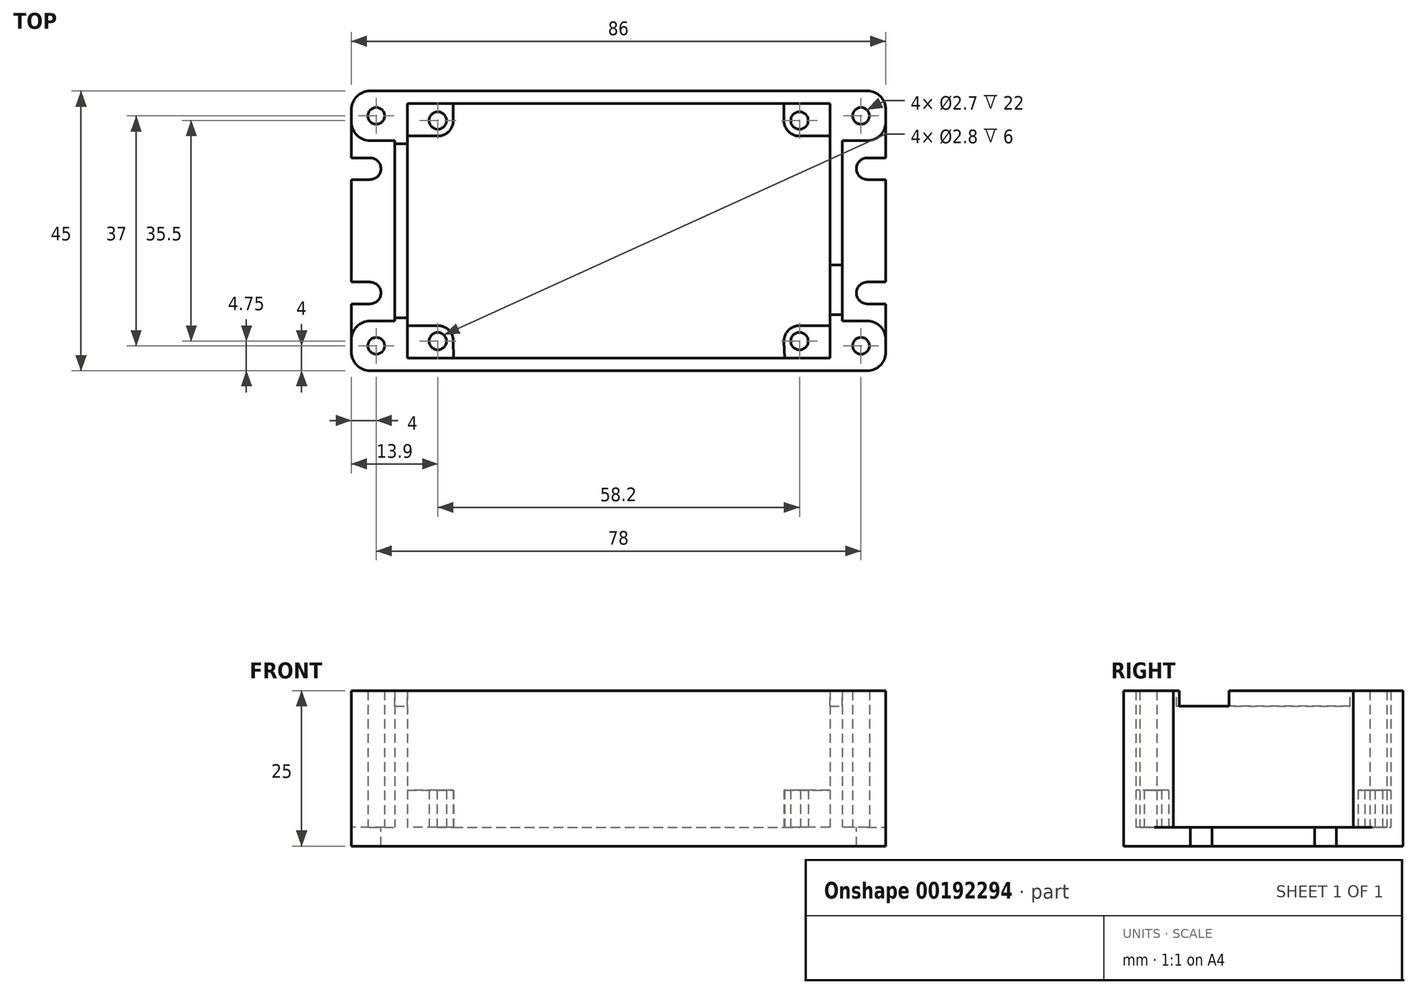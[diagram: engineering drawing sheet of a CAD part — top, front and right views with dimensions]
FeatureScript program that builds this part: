
annotation { "Feature Type Name" : "Feature", "Feature Type Description" : "" }
export const myFeature = defineFeature(function(context is Context, id is Id, definition is map)
    precondition{}
    {
        {
            var Q0;
            Q0=qCreatedBy(makeId("Top.planeOp"),FACE);
            var sketch = newSketch(context, id + "F0", { "sketchPlane" : qUnion([Q0])});
            skLineSegment(sketch, "E0.bottom", {"start": v(-43, 22.5) * mm, "end": v(43, 22.5) * mm});
            skLineSegment(sketch, "E0.top", {"start": v(-43, -22.5) * mm, "end": v(43, -22.5) * mm});
            skLineSegment(sketch, "E0.left", {"start": v(-43, 22.5) * mm, "end": v(-43, -22.5) * mm});
            skLineSegment(sketch, "E0.right", {"start": v(43, 22.5) * mm, "end": v(43, -22.5) * mm});
            skSolve(sketch);
        }
        {
            var Q0;
            Q0 = qSketchRegion(id + "F0", true);
            extrude(context, id + "F1", {"entities" : qUnion([Q0]), "depth" : 3 * mm});
        }
        {
            var Q0;
            Q0=makeQuery(id+"F1.opExtrude","CAP_FACE",FACE,{"disambiguationData":[OSD([sQuery(id+"F0.wireOp",EDGE,"E0.bottom"),sQuery(id+"F0.wireOp",EDGE,"E0.top"),sQuery(id+"F0.wireOp",EDGE,"E0.left"),sQuery(id+"F0.wireOp",EDGE,"E0.right")])],"isStart":false});
            var sketch = newSketch(context, id + "F2", { "sketchPlane" : qUnion([Q0])});
            skLineSegment(sketch, "E1.bottom", {"start": v(-36, 22.5) * mm, "end": v(36, 22.5) * mm, "construction": true});
            skLineSegment(sketch, "E1.top", {"start": v(-36, -22.5) * mm, "end": v(36, -22.5) * mm, "construction": true});
            skLineSegment(sketch, "E1.left", {"start": v(-36, 22.5) * mm, "end": v(-36, -22.5) * mm, "construction": true});
            skLineSegment(sketch, "E1.right", {"start": v(36, 22.5) * mm, "end": v(36, -22.5) * mm, "construction": true});
            skLineSegment(sketch, "E2.0", {"start": v(-34, 20.5) * mm, "end": v(34, 20.5) * mm});
            skLineSegment(sketch, "E2.1", {"start": v(-34, 20.5) * mm, "end": v(-34, -20.5) * mm});
            skLineSegment(sketch, "E2.2", {"start": v(-34, -20.5) * mm, "end": v(34, -20.5) * mm});
            skLineSegment(sketch, "E2.3", {"start": v(34, 20.5) * mm, "end": v(34, -20.5) * mm});
            skLineSegment(sketch, "E3", {"start": v(-43, 22.5) * mm, "end": v(43, 22.5) * mm});
            skLineSegment(sketch, "E4", {"start": v(43, 22.5) * mm, "end": v(43, 14.5) * mm});
            skLineSegment(sketch, "E5", {"start": v(43, 14.5) * mm, "end": v(36, 14.5) * mm});
            skLineSegment(sketch, "E6", {"start": v(36, 14.5) * mm, "end": v(36, -14.5) * mm});
            skLineSegment(sketch, "E7", {"start": v(36, -14.5) * mm, "end": v(43, -14.5) * mm});
            skLineSegment(sketch, "E8", {"start": v(43, -14.5) * mm, "end": v(43, -22.5) * mm});
            skLineSegment(sketch, "E9", {"start": v(43, -22.5) * mm, "end": v(-43, -22.5) * mm});
            skLineSegment(sketch, "E10", {"start": v(-43, -22.5) * mm, "end": v(-43, -14.5) * mm});
            skLineSegment(sketch, "E11", {"start": v(-43, -14.5) * mm, "end": v(-36, -14.5) * mm});
            skLineSegment(sketch, "E12", {"start": v(-36, -14.5) * mm, "end": v(-36, 14.5) * mm});
            skLineSegment(sketch, "E13", {"start": v(-36, 14.5) * mm, "end": v(-43, 14.5) * mm});
            skLineSegment(sketch, "E14", {"start": v(-43, 14.5) * mm, "end": v(-43, 22.5) * mm});
            skLineSegment(sketch, "E15", {"start": v(-39, 29.97) * mm, "end": v(-39, -31.03) * mm, "construction": true});
            skCircle(sketch, "E16", {"center": v(-39, 18.5) * mm, "radius": 1.35 * mm});
            skCircle(sketch, "E17", {"center": v(-39, -18.5) * mm, "radius": 1.35 * mm});
            skCircle(sketch, "E18.MirrorC", {"center": v(39, -18.5) * mm, "radius": 1.35 * mm});
            skCircle(sketch, "E19.MirrorC", {"center": v(39, 18.5) * mm, "radius": 1.35 * mm});
            skSolve(sketch);
        }
        {
            var Q0;
            Q0 = qSketchRegion(id + "F2", true);
            extrude(context, id + "F3", {"entities" : qUnion([Q0]), "operationType" : NewBodyOperationType.ADD, "depth" : 22 * mm});
        }
        {
            var Q0;
            Q0=makeQuery(id+"F3.boolean.opBoolean","SPLIT",FACE,{"disambiguationData":[TD([makeQuery(id+"F3.opExtrude","SWEPT_FACE",FACE,{"disambiguationData":[OSD([sQuery(id+"F2.wireOp",EDGE,"E2.0")])]})])],"derivedFrom":makeQuery(id+"F1.opExtrude","CAP_FACE",FACE,{"disambiguationData":[OSD([sQuery(id+"F0.wireOp",EDGE,"E0.bottom"),sQuery(id+"F0.wireOp",EDGE,"E0.top"),sQuery(id+"F0.wireOp",EDGE,"E0.left"),sQuery(id+"F0.wireOp",EDGE,"E0.right")])],"isStart":false})});
            var sketch = newSketch(context, id + "F4", { "sketchPlane" : qUnion([Q0])});
            skCircle(sketch, "E20", {"center": v(-29.1, 17.75) * mm, "radius": 1.4 * mm});
            skCircle(sketch, "E21", {"center": v(-29.1, -17.75) * mm, "radius": 1.4 * mm});
            skCircle(sketch, "E22.MirrorC", {"center": v(29.1, 17.75) * mm, "radius": 1.4 * mm});
            skCircle(sketch, "E23.MirrorC", {"center": v(29.1, -17.75) * mm, "radius": 1.4 * mm});
            skArc(sketch, "E24", {"start": v(-29.26, 15.26) * mm, "mid": v(-27.32, 16) * mm, "end": v(-26.6, 17.95) * mm});
            skArc(sketch, "E25", {"start": v(-26.6, -17.7) * mm, "mid": v(-27.41, -15.9) * mm, "end": v(-29.26, -15.26) * mm});
            skArc(sketch, "E26", {"start": v(26.6, 17.95) * mm, "mid": v(27.26, 16.05) * mm, "end": v(29.1, 15.25) * mm});
            skArc(sketch, "E27", {"start": v(29.25, -15.25) * mm, "mid": v(27.34, -15.97) * mm, "end": v(26.6, -17.88) * mm});
            skLineSegment(sketch, "E28", {"start": v(-26.6, 17.55) * mm, "end": v(-26.6, 20.5) * mm});
            skLineSegment(sketch, "E29", {"start": v(-28.94, 15.26) * mm, "end": v(-34, 15.26) * mm});
            skLineSegment(sketch, "E30", {"start": v(-34, 15.26) * mm, "end": v(-34, 20.5) * mm});
            skLineSegment(sketch, "E31", {"start": v(-34, 20.5) * mm, "end": v(-26.6, 20.5) * mm});
            skLineSegment(sketch, "E32", {"start": v(26.6, 17.55) * mm, "end": v(26.6, 20.5) * mm});
            skLineSegment(sketch, "E33", {"start": v(26.6, 20.5) * mm, "end": v(34, 20.5) * mm});
            skLineSegment(sketch, "E34", {"start": v(34, 20.5) * mm, "end": v(34, 15.26) * mm});
            skLineSegment(sketch, "E35", {"start": v(34, 15.26) * mm, "end": v(29.1, 15.25) * mm});
            skLineSegment(sketch, "E36", {"start": v(-28.94, -15.26) * mm, "end": v(-34, -15.26) * mm});
            skLineSegment(sketch, "E37", {"start": v(-34, -15.26) * mm, "end": v(-34, -20.5) * mm});
            skLineSegment(sketch, "E38", {"start": v(-26.6, -17.7) * mm, "end": v(-26.54, -20.5) * mm});
            skLineSegment(sketch, "E39", {"start": v(-26.54, -20.5) * mm, "end": v(-34, -20.5) * mm});
            skLineSegment(sketch, "E40", {"start": v(26.6, -17.88) * mm, "end": v(26.74, -20.5) * mm});
            skPoint(sketch, "E40.startSnap0", {"position": v(-34, -17.88) * mm});
            skLineSegment(sketch, "E41", {"start": v(26.74, -20.5) * mm, "end": v(34, -20.5) * mm});
            skLineSegment(sketch, "E42", {"start": v(34, -20.5) * mm, "end": v(34, -15.26) * mm});
            skLineSegment(sketch, "E43", {"start": v(34, -15.26) * mm, "end": v(28.95, -15.25) * mm});
            skSolve(sketch);
        }
        {
            var Q0;
            Q0 = qSketchRegion(id + "F4", true);
            extrude(context, id + "F5", {"entities" : qUnion([Q0]), "operationType" : NewBodyOperationType.ADD, "depth" : 6 * mm});
        }
        {
            var Q0;
            {var subQ0=sQuery(id+"F0.wireOp",EDGE,"E0.left");Q0=makeQuery(id+"F3.boolean.opBoolean","SPLIT",FACE,{"disambiguationData":[TD([makeQuery(id+"F1.opExtrude","SWEPT_FACE",FACE,{"disambiguationData":[OSD([subQ0])]})])],"derivedFrom":makeQuery(id+"F1.opExtrude","CAP_FACE",FACE,{"disambiguationData":[OSD([sQuery(id+"F0.wireOp",EDGE,"E0.bottom"),sQuery(id+"F0.wireOp",EDGE,"E0.top"),subQ0,sQuery(id+"F0.wireOp",EDGE,"E0.right")])],"isStart":false})});}
            var sketch = newSketch(context, id + "F6", { "sketchPlane" : qUnion([Q0])});
            skLineSegment(sketch, "E44", {"start": v(-40, 29.83) * mm, "end": v(-40, -29.78) * mm, "construction": true});
            skArc(sketch, "E45", {"start": v(-40, 8.25) * mm, "mid": v(-38.25, 10) * mm, "end": v(-40, 11.75) * mm});
            skArc(sketch, "E46", {"start": v(-40, -11.75) * mm, "mid": v(-38.25, -10) * mm, "end": v(-40, -8.25) * mm});
            skLineSegment(sketch, "E47", {"start": v(-40, 11.75) * mm, "end": v(-43, 11.75) * mm});
            skLineSegment(sketch, "E48", {"start": v(-40, 8.25) * mm, "end": v(-43, 8.25) * mm});
            skLineSegment(sketch, "E49", {"start": v(-43, 8.25) * mm, "end": v(-43, 11.75) * mm});
            skLineSegment(sketch, "E50", {"start": v(-40, -8.25) * mm, "end": v(-43, -8.25) * mm});
            skLineSegment(sketch, "E51", {"start": v(-40, -11.75) * mm, "end": v(-43, -11.75) * mm});
            skLineSegment(sketch, "E52", {"start": v(-43, -11.75) * mm, "end": v(-43, -8.25) * mm});
            skArc(sketch, "E53.MirrorCS", {"start": v(40, 8.25) * mm, "mid": v(38.25, 10) * mm, "end": v(40, 11.75) * mm});
            skLineSegment(sketch, "E54.MirrorCS", {"start": v(40, 11.75) * mm, "end": v(43, 11.75) * mm});
            skLineSegment(sketch, "E55.MirrorCS", {"start": v(43, 8.25) * mm, "end": v(43, 11.75) * mm});
            skLineSegment(sketch, "E56.MirrorCS", {"start": v(40, 8.25) * mm, "end": v(43, 8.25) * mm});
            skArc(sketch, "E57.MirrorCS", {"start": v(40, -11.75) * mm, "mid": v(38.25, -10) * mm, "end": v(40, -8.25) * mm});
            skLineSegment(sketch, "E58.MirrorCS", {"start": v(40, -8.25) * mm, "end": v(43, -8.25) * mm});
            skLineSegment(sketch, "E59.MirrorCS", {"start": v(43, -11.75) * mm, "end": v(43, -8.25) * mm});
            skLineSegment(sketch, "E60.MirrorCS", {"start": v(40, -11.75) * mm, "end": v(43, -11.75) * mm});
            skSolve(sketch);
        }
        {
            var Q0;
            Q0 = qSketchRegion(id + "F6", true);
            extrude(context, id + "F7", {"entities" : qUnion([Q0]), "operationType" : NewBodyOperationType.REMOVE, "endBound" : BoundingType.THROUGH_ALL, "oppositeDirection" : true, "depth" : 25 * mm});
        }
        {
            var Q0;
            Q0=makeQuery(id+"F3.boolean.opBoolean","MERGE",EDGE,{"derivedFrom":[makeQuery(id+"F1.opExtrude","SWEPT_EDGE",EDGE,{"disambiguationData":[OSD([sQuery(id+"F0.wireOp",EDGE,"E0.top"),sQuery(id+"F0.wireOp",EDGE,"E0.left")])]}),makeQuery(id+"F3.opExtrude","SWEPT_EDGE",EDGE,{"disambiguationData":[OSD([sQuery(id+"F2.wireOp",EDGE,"E9"),sQuery(id+"F2.wireOp",EDGE,"E10")])]})]});
            var Q1;
            Q1=makeQuery(id+"F3.opExtrude","SWEPT_EDGE",EDGE,{"disambiguationData":[OSD([sQuery(id+"F0.wireOp",EDGE,"E0.left"),sQuery(id+"F2.wireOp",EDGE,"E13"),sQuery(id+"F2.wireOp",EDGE,"E14")])]});
            var Q2;
            Q2=makeQuery(id+"F3.boolean.opBoolean","MERGE",EDGE,{"derivedFrom":[makeQuery(id+"F1.opExtrude","SWEPT_EDGE",EDGE,{"disambiguationData":[OSD([sQuery(id+"F0.wireOp",EDGE,"E0.bottom"),sQuery(id+"F0.wireOp",EDGE,"E0.left")])]}),makeQuery(id+"F3.opExtrude","SWEPT_EDGE",EDGE,{"disambiguationData":[OSD([sQuery(id+"F2.wireOp",EDGE,"E3"),sQuery(id+"F2.wireOp",EDGE,"E14")])]})]});
            var Q3;
            Q3=makeQuery(id+"F3.opExtrude","SWEPT_EDGE",EDGE,{"disambiguationData":[OSD([sQuery(id+"F0.wireOp",EDGE,"E0.left"),sQuery(id+"F2.wireOp",EDGE,"E10"),sQuery(id+"F2.wireOp",EDGE,"E11")])]});
            var Q4;
            Q4=makeQuery(id+"F3.boolean.opBoolean","MERGE",EDGE,{"derivedFrom":[makeQuery(id+"F1.opExtrude","SWEPT_EDGE",EDGE,{"disambiguationData":[OSD([sQuery(id+"F0.wireOp",EDGE,"E0.top"),sQuery(id+"F0.wireOp",EDGE,"E0.right")])]}),makeQuery(id+"F3.opExtrude","SWEPT_EDGE",EDGE,{"disambiguationData":[OSD([sQuery(id+"F2.wireOp",EDGE,"E8"),sQuery(id+"F2.wireOp",EDGE,"E9")])]})]});
            var Q5;
            Q5=makeQuery(id+"F3.opExtrude","SWEPT_EDGE",EDGE,{"disambiguationData":[OSD([sQuery(id+"F0.wireOp",EDGE,"E0.right"),sQuery(id+"F2.wireOp",EDGE,"E7"),sQuery(id+"F2.wireOp",EDGE,"E8")])]});
            var Q6;
            Q6=makeQuery(id+"F3.opExtrude","SWEPT_EDGE",EDGE,{"disambiguationData":[OSD([sQuery(id+"F0.wireOp",EDGE,"E0.right"),sQuery(id+"F2.wireOp",EDGE,"E4"),sQuery(id+"F2.wireOp",EDGE,"E5")])]});
            var Q7;
            Q7=makeQuery(id+"F3.boolean.opBoolean","MERGE",EDGE,{"derivedFrom":[makeQuery(id+"F1.opExtrude","SWEPT_EDGE",EDGE,{"disambiguationData":[OSD([sQuery(id+"F0.wireOp",EDGE,"E0.bottom"),sQuery(id+"F0.wireOp",EDGE,"E0.right")])]}),makeQuery(id+"F3.opExtrude","SWEPT_EDGE",EDGE,{"disambiguationData":[OSD([sQuery(id+"F2.wireOp",EDGE,"E3"),sQuery(id+"F2.wireOp",EDGE,"E4")])]})]});
            fillet(context, id + "F8", {"entities" : qUnion([Q0, Q1, Q2, Q3, Q4, Q5, Q6, Q7]), "radius" : 3 * mm, "tangentPropagation" : true, "allowEdgeOverflow" : false});
        }
        {
            var Q0;
            Q0=makeQuery(id+"F3.opExtrude","CAP_FACE",FACE,{"disambiguationData":[OSD([sQuery(id+"F2.wireOp",EDGE,"E2.0"),sQuery(id+"F2.wireOp",EDGE,"E2.1"),sQuery(id+"F2.wireOp",EDGE,"E2.2"),sQuery(id+"F2.wireOp",EDGE,"E2.3"),sQuery(id+"F2.wireOp",EDGE,"E3"),sQuery(id+"F2.wireOp",EDGE,"E4"),sQuery(id+"F2.wireOp",EDGE,"E5"),sQuery(id+"F2.wireOp",EDGE,"E6"),sQuery(id+"F2.wireOp",EDGE,"E7"),sQuery(id+"F2.wireOp",EDGE,"E8"),sQuery(id+"F2.wireOp",EDGE,"E9"),sQuery(id+"F2.wireOp",EDGE,"E10"),sQuery(id+"F2.wireOp",EDGE,"E11"),sQuery(id+"F2.wireOp",EDGE,"E12"),sQuery(id+"F2.wireOp",EDGE,"E13"),sQuery(id+"F2.wireOp",EDGE,"E14"),sQuery(id+"F2.wireOp",EDGE,"E16"),sQuery(id+"F2.wireOp",EDGE,"E17"),sQuery(id+"F2.wireOp",EDGE,"E18.MirrorC"),sQuery(id+"F2.wireOp",EDGE,"E19.MirrorC")])],"isStart":false});
            var sketch = newSketch(context, id + "F9", { "sketchPlane" : qUnion([Q0])});
            skLineSegment(sketch, "E61.bottom", {"start": v(-36, 14) * mm, "end": v(-34, 14) * mm});
            skLineSegment(sketch, "E61.top", {"start": v(-36, -14) * mm, "end": v(-34, -14) * mm});
            skLineSegment(sketch, "E61.left", {"start": v(-36, 14) * mm, "end": v(-36, -14) * mm});
            skLineSegment(sketch, "E61.right", {"start": v(-34, 14) * mm, "end": v(-34, -14) * mm});
            skLineSegment(sketch, "E62.bottom", {"start": v(34, -5.5) * mm, "end": v(36, -5.5) * mm});
            skLineSegment(sketch, "E62.top", {"start": v(34, -13.5) * mm, "end": v(36, -13.5) * mm});
            skLineSegment(sketch, "E62.left", {"start": v(34, -5.5) * mm, "end": v(34, -13.5) * mm});
            skLineSegment(sketch, "E62.right", {"start": v(36, -5.5) * mm, "end": v(36, -13.5) * mm});
            skLineSegment(sketch, "E63", {"start": v(15.76, -9.5) * mm, "end": v(48.31, -9.5) * mm, "construction": true});
            skSolve(sketch);
        }
        {
            var Q0;
            Q0 = qSketchRegion(id + "F9", true);
            extrude(context, id + "F10", {"entities" : qUnion([Q0]), "operationType" : NewBodyOperationType.REMOVE, "oppositeDirection" : true, "depth" : 2.5 * mm});
        }
    });
